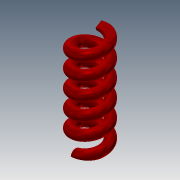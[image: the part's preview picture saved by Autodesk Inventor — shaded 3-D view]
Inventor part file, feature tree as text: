
AUTODESK INVENTOR PART (.ipt)
format: ipt  version: 2015 (Build 190159000, 159)  size: 220,672 bytes
history: native  units: mm
features: sketch x2, extrude x1, helix x1, projected_geometry x1
ambient origin geometry x8: Origin, YZ Plane, XZ Plane, XY Plane, X Axis, Y Axis, Z Axis, Center Point
bodies: Solid1 (feature_tree)
feature tree (5):
  extrude  "Extrusion1"  Depth=100.0mm TaperAngle=0.0deg
  helix  "Coil1"  [1 undecoded]
  sketch  "Sketch1"  dims[d0=45.0mm d1=100.0mm d2=0.0mm d3=100.0mm]
  sketch  "Sketch2"  dims[d4=8.0mm d5=17.0mm d6=18.0mm d7=100.0mm d8=40.0mm d9=0.0mm d10=90.0deg d11=90.0deg d12=0.0mm d13=0.0mm]
  projected_geometry  "Projected Loop1"
note: 1 required parameter value undecoded (feature->parameter linkage not recoverable at this tier; creation-order binding heuristic only, values carry confidence <= 0.55)
